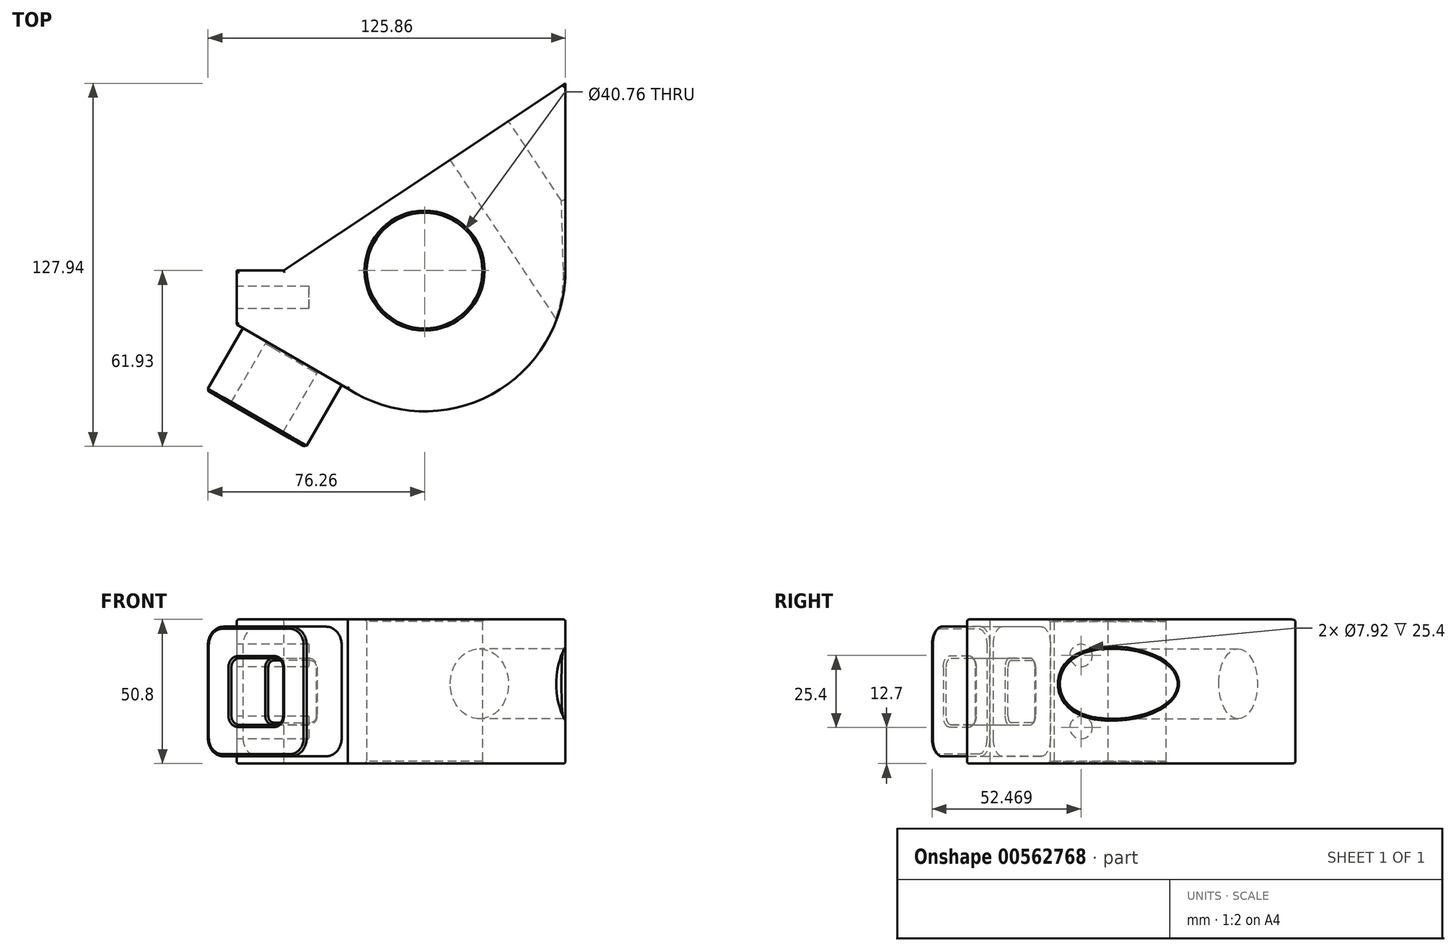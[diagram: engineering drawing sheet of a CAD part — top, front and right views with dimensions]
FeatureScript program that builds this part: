
annotation { "Feature Type Name" : "Feature", "Feature Type Description" : "" }
export const myFeature = defineFeature(function(context is Context, id is Id, definition is map)
    precondition{}
    {
        {
            var Q0;
            Q0=qCreatedBy(makeId("Top.planeOp"),FACE);
            var sketch = newSketch(context, id + "F0", { "sketchPlane" : qUnion([Q0])});
            skCircle(sketch, "E0", {"center": v(0, 0) * mm, "radius": 20.38 * mm});
            skArc(sketch, "E1", {"start": v(-27.02, -41.59) * mm, "mid": v(23.66, -43.59) * mm, "end": v(49.6, 0) * mm});
            skLineSegment(sketch, "E2", {"start": v(0, 0) * mm, "end": v(49.6, 0) * mm});
            skLineSegment(sketch, "E3", {"start": v(49.6, 0) * mm, "end": v(49.6, 66) * mm});
            skLineSegment(sketch, "E4", {"start": v(49.6, 66) * mm, "end": v(-49.6, 0) * mm});
            skLineSegment(sketch, "E5", {"start": v(-49.6, 0) * mm, "end": v(-66.14, 0) * mm});
            skLineSegment(sketch, "E6", {"start": v(-66.14, 0) * mm, "end": v(-66.14, -19) * mm});
            skLineSegment(sketch, "E7", {"start": v(-66.14, -19) * mm, "end": v(-27.02, -41.59) * mm});
            skSolve(sketch);
        }
        {
            var Q0;
            Q0 = qSketchRegion(id + "F0", true);
            extrude(context, id + "F1", {"entities" : qUnion([Q0]), "depth" : 50.8 * mm, "offsetDistance" : 25.4 * mm});
        }
        {
            var Q0;
            Q0=makeQuery(id+"F1.opExtrude","SWEPT_FACE",FACE,{"disambiguationData":[OSD([sQuery(id+"F0.wireOp",EDGE,"E4")])]});
            var sketch = newSketch(context, id + "F2", { "sketchPlane" : qUnion([Q0])});
            skCircle(sketch, "E8", {"center": v(-41.47, 28.13) * mm, "radius": 12.31 * mm});
            skSolve(sketch);
        }
        {
            var Q0;
            Q0=makeQuery(id+"F2.imprint","IMPRINT",FACE,{"disambiguationData":[TD([[makeQuery(id+"F2.imprint","IMPRINT",EDGE,{"derivedFrom":sQuery(id+"F2.wireOp",EDGE,"E8")}),1.0]])]});
            extrude(context, id + "F3", {"entities" : qUnion([Q0]), "operationType" : NewBodyOperationType.REMOVE, "oppositeDirection" : true, "depth" : 76.2 * mm, "offsetDistance" : 25.4 * mm});
        }
        {
            var Q0;
            Q0=makeQuery(id+"F1.opExtrude","SWEPT_FACE",FACE,{"disambiguationData":[OSD([sQuery(id+"F0.wireOp",EDGE,"E7")])]});
            var sketch = newSketch(context, id + "F4", { "sketchPlane" : qUnion([Q0])});
            skLineSegment(sketch, "E9", {"start": v(-45.24, 41.91) * mm, "end": v(-45.24, 8.89) * mm});
            skLineSegment(sketch, "E10", {"start": v(-38.89, 2.54) * mm, "end": v(-11.5, 2.54) * mm});
            skLineSegment(sketch, "E11", {"start": v(-5.14, 8.9) * mm, "end": v(-5.14, 41.91) * mm});
            skLineSegment(sketch, "E12", {"start": v(-11.5, 48.26) * mm, "end": v(-38.89, 48.26) * mm});
            skPoint(sketch, "E13.visualSharp", {"position": v(-45.24, 48.26) * mm});
            skArc(sketch, "E13.filletArc", {"start": v(-38.89, 48.26) * mm, "mid": v(-43.38, 46.4) * mm, "end": v(-45.24, 41.91) * mm});
            skPoint(sketch, "E14.visualSharp", {"position": v(-5.14, 48.26) * mm});
            skArc(sketch, "E14.filletArc", {"start": v(-5.14, 41.91) * mm, "mid": v(-7, 46.4) * mm, "end": v(-11.5, 48.26) * mm});
            skPoint(sketch, "E15.visualSharp", {"position": v(-45.24, 2.54) * mm});
            skArc(sketch, "E15.filletArc", {"start": v(-45.24, 8.89) * mm, "mid": v(-43.38, 4.4) * mm, "end": v(-38.89, 2.54) * mm});
            skPoint(sketch, "E16.visualSharp", {"position": v(-5.14, 2.54) * mm});
            skArc(sketch, "E16.filletArc", {"start": v(-11.5, 2.54) * mm, "mid": v(-7, 4.4) * mm, "end": v(-5.14, 8.9) * mm});
            skLineSegment(sketch, "E17.bottom", {"start": v(-32.54, 37.14) * mm, "end": v(-17.84, 37.14) * mm});
            skLineSegment(sketch, "E17.top", {"start": v(-32.54, 13.67) * mm, "end": v(-17.84, 13.67) * mm});
            skLineSegment(sketch, "E17.left", {"start": v(-35.71, 33.97) * mm, "end": v(-35.71, 16.84) * mm});
            skLineSegment(sketch, "E17.right", {"start": v(-14.67, 33.97) * mm, "end": v(-14.67, 16.84) * mm});
            skPoint(sketch, "E18.visualSharp", {"position": v(-35.71, 37.14) * mm});
            skArc(sketch, "E18.filletArc", {"start": v(-32.54, 37.14) * mm, "mid": v(-34.78, 36.21) * mm, "end": v(-35.71, 33.97) * mm});
            skPoint(sketch, "E19.visualSharp", {"position": v(-14.67, 37.14) * mm});
            skArc(sketch, "E19.filletArc", {"start": v(-14.67, 33.97) * mm, "mid": v(-15.6, 36.21) * mm, "end": v(-17.84, 37.14) * mm});
            skPoint(sketch, "E20.visualSharp", {"position": v(-35.71, 13.67) * mm});
            skArc(sketch, "E20.filletArc", {"start": v(-35.71, 16.84) * mm, "mid": v(-34.78, 14.6) * mm, "end": v(-32.54, 13.67) * mm});
            skPoint(sketch, "E21.visualSharp", {"position": v(-14.67, 13.67) * mm});
            skArc(sketch, "E21.filletArc", {"start": v(-17.84, 13.67) * mm, "mid": v(-15.6, 14.6) * mm, "end": v(-14.67, 16.84) * mm});
            skSolve(sketch);
        }
        {
            var Q0;
            Q0 = qSketchRegion(id + "F4", true);
            extrude(context, id + "F5", {"entities" : qUnion([Q0]), "operationType" : NewBodyOperationType.ADD, "depth" : 25.4 * mm, "offsetDistance" : 25.4 * mm});
        }
        {
            var Q0;
            Q0=makeQuery(id+"F1.opExtrude","SWEPT_FACE",FACE,{"disambiguationData":[OSD([sQuery(id+"F0.wireOp",EDGE,"E6")])]});
            var sketch = newSketch(context, id + "F6", { "sketchPlane" : qUnion([Q0])});
            skCircle(sketch, "E22", {"center": v(9.46, 38.1) * mm, "radius": 3.96 * mm});
            skCircle(sketch, "E23", {"center": v(9.46, 12.7) * mm, "radius": 3.96 * mm});
            skLineSegment(sketch, "E24", {"start": v(9.46, 38.1) * mm, "end": v(9.46, 12.7) * mm});
            skSolve(sketch);
        }
        {
            var Q0;
            Q0=makeQuery(id+"F6.imprint","IMPRINT",FACE,{"disambiguationData":[TD([[makeQuery(id+"F6.imprint","IMPRINT",EDGE,{"derivedFrom":sQuery(id+"F6.wireOp",EDGE,"E23")}),1.0]])]});
            var Q1;
            Q1=makeQuery(id+"F6.imprint","IMPRINT",FACE,{"disambiguationData":[TD([[makeQuery(id+"F6.imprint","IMPRINT",EDGE,{"derivedFrom":sQuery(id+"F6.wireOp",EDGE,"E22")}),1.0]])]});
            var Q2;
            Q2=sQuery(id+"F6.wireOp",EDGE,"E22");
            var Q3;
            Q3=sQuery(id+"F6.wireOp",EDGE,"E23");
            extrude(context, id + "F7", {"entities" : qUnion([Q0, Q1]), "operationType" : NewBodyOperationType.REMOVE, "surfaceEntities" : qUnion([Q2, Q3]), "oppositeDirection" : true, "depth" : 25.4 * mm, "offsetDistance" : 25.4 * mm});
        }
        {
            var Q0;
            Q0=makeQuery(id+"F7.boolean.opBoolean","COPY",EDGE,{"derivedFrom":makeQuery(id+"F7.opExtrude","CAP_EDGE",EDGE,{"disambiguationData":[OSD([sQuery(id+"F6.wireOp",EDGE,"E23")])],"isStart":true})});
            var Q1;
            Q1=makeQuery(id+"F7.boolean.opBoolean","COPY",EDGE,{"derivedFrom":makeQuery(id+"F7.opExtrude","CAP_EDGE",EDGE,{"disambiguationData":[OSD([sQuery(id+"F6.wireOp",EDGE,"E22")])],"isStart":true})});
            var Q2;
            Q2=makeQuery(id+"F5.opExtrude","CAP_EDGE",EDGE,{"disambiguationData":[OSD([sQuery(id+"F4.wireOp",EDGE,"E17.top")])],"isStart":false});
            var Q3;
            Q3=makeQuery(id+"F5.opExtrude","CAP_EDGE",EDGE,{"disambiguationData":[OSD([sQuery(id+"F4.wireOp",EDGE,"E21.filletArc")])],"isStart":false});
            var Q4;
            Q4=makeQuery(id+"F5.opExtrude","CAP_EDGE",EDGE,{"disambiguationData":[OSD([sQuery(id+"F4.wireOp",EDGE,"E12")])],"isStart":false});
            var Q5;
            Q5=makeQuery(id+"F5.opExtrude","CAP_EDGE",EDGE,{"disambiguationData":[OSD([sQuery(id+"F4.wireOp",EDGE,"E13.filletArc")])],"isStart":false});
            var Q6;
            Q6=makeQuery(id+"F5.boolean.opBoolean","SPLIT",FACE,{"disambiguationData":[TD([makeQuery(id+"F5.opExtrude","SWEPT_FACE",FACE,{"disambiguationData":[OSD([sQuery(id+"F4.wireOp",EDGE,"E17.bottom")])]})])],"derivedFrom":makeQuery(id+"F1.opExtrude","SWEPT_FACE",FACE,{"disambiguationData":[OSD([sQuery(id+"F0.wireOp",EDGE,"E7")])]})});
            var Q7;
            Q7=makeQuery(id+"F1.opExtrude","CAP_EDGE",EDGE,{"disambiguationData":[OSD([sQuery(id+"F0.wireOp",EDGE,"E0")])],"isStart":false});
            var Q8;
            Q8=makeQuery(id+"F3.boolean.opBoolean","INTERSECT",EDGE,{"derivedFrom":[makeQuery(id+"F1.opExtrude","SWEPT_FACE",FACE,{"disambiguationData":[OSD([sQuery(id+"F0.wireOp",EDGE,"E3")])]}),makeQuery(id+"F3.opExtrude","SWEPT_FACE",FACE,{"disambiguationData":[OSD([sQuery(id+"F2.wireOp",EDGE,"E8")])]})]});
            var Q9;
            Q9=makeQuery(id+"F3.boolean.opBoolean","INTERSECT",EDGE,{"derivedFrom":[makeQuery(id+"F1.opExtrude","SWEPT_FACE",FACE,{"disambiguationData":[OSD([sQuery(id+"F0.wireOp",EDGE,"E1")])]}),makeQuery(id+"F3.opExtrude","SWEPT_FACE",FACE,{"disambiguationData":[OSD([sQuery(id+"F2.wireOp",EDGE,"E8")])]})]});
            var Q10;
            Q10=makeQuery(id+"F1.opExtrude","CAP_EDGE",EDGE,{"disambiguationData":[OSD([sQuery(id+"F0.wireOp",EDGE,"E0")])],"isStart":true});
            var Q11;
            Q11=makeQuery(id+"F3.boolean.opBoolean","COPY",EDGE,{"derivedFrom":makeQuery(id+"F3.opExtrude","CAP_EDGE",EDGE,{"disambiguationData":[OSD([sQuery(id+"F2.wireOp",EDGE,"E8")])],"isStart":true})});
            chamfer(context, id + "F8", {"entities" : qUnion([Q0, Q1, Q2, Q3, Q4, Q5, Q6, Q7, Q8, Q9, Q10, Q11]), "width" : 0.76 * mm, "tangentPropagation" : true});
        }
        {
            var Q0;
            Q0=makeQuery(id+"F1.opExtrude","CAP_EDGE",EDGE,{"disambiguationData":[OSD([sQuery(id+"F0.wireOp",EDGE,"E1")])],"isStart":false});
            var Q1;
            Q1=makeQuery(id+"F1.opExtrude","CAP_EDGE",EDGE,{"disambiguationData":[OSD([sQuery(id+"F0.wireOp",EDGE,"E6")])],"isStart":false});
            var Q2;
            Q2=makeQuery(id+"F1.opExtrude","CAP_EDGE",EDGE,{"disambiguationData":[OSD([sQuery(id+"F0.wireOp",EDGE,"E5")])],"isStart":false});
            var Q3;
            Q3=makeQuery(id+"F1.opExtrude","CAP_EDGE",EDGE,{"disambiguationData":[OSD([sQuery(id+"F0.wireOp",EDGE,"E4")])],"isStart":false});
            var Q4;
            Q4=makeQuery(id+"F1.opExtrude","CAP_EDGE",EDGE,{"disambiguationData":[OSD([sQuery(id+"F0.wireOp",EDGE,"E3")])],"isStart":false});
            var Q5;
            Q5=makeQuery(id+"F1.opExtrude","CAP_EDGE",EDGE,{"disambiguationData":[OSD([sQuery(id+"F0.wireOp",EDGE,"E6")])],"isStart":true});
            var Q6;
            Q6=makeQuery(id+"F1.opExtrude","CAP_EDGE",EDGE,{"disambiguationData":[OSD([sQuery(id+"F0.wireOp",EDGE,"E4")])],"isStart":true});
            var Q7;
            Q7=makeQuery(id+"F1.opExtrude","CAP_EDGE",EDGE,{"disambiguationData":[OSD([sQuery(id+"F0.wireOp",EDGE,"E3")])],"isStart":true});
            var Q8;
            Q8=makeQuery(id+"F1.opExtrude","CAP_EDGE",EDGE,{"disambiguationData":[OSD([sQuery(id+"F0.wireOp",EDGE,"E1")])],"isStart":true});
            var Q9;
            Q9=makeQuery(id+"F1.opExtrude","CAP_EDGE",EDGE,{"disambiguationData":[OSD([sQuery(id+"F0.wireOp",EDGE,"E5")])],"isStart":true});
            fillet(context, id + "F9", {"entities" : qUnion([Q0, Q1, Q2, Q3, Q4, Q5, Q6, Q7, Q8, Q9]), "radius" : 0.76 * mm, "tangentPropagation" : true, "allowEdgeOverflow" : false});
        }
    });
